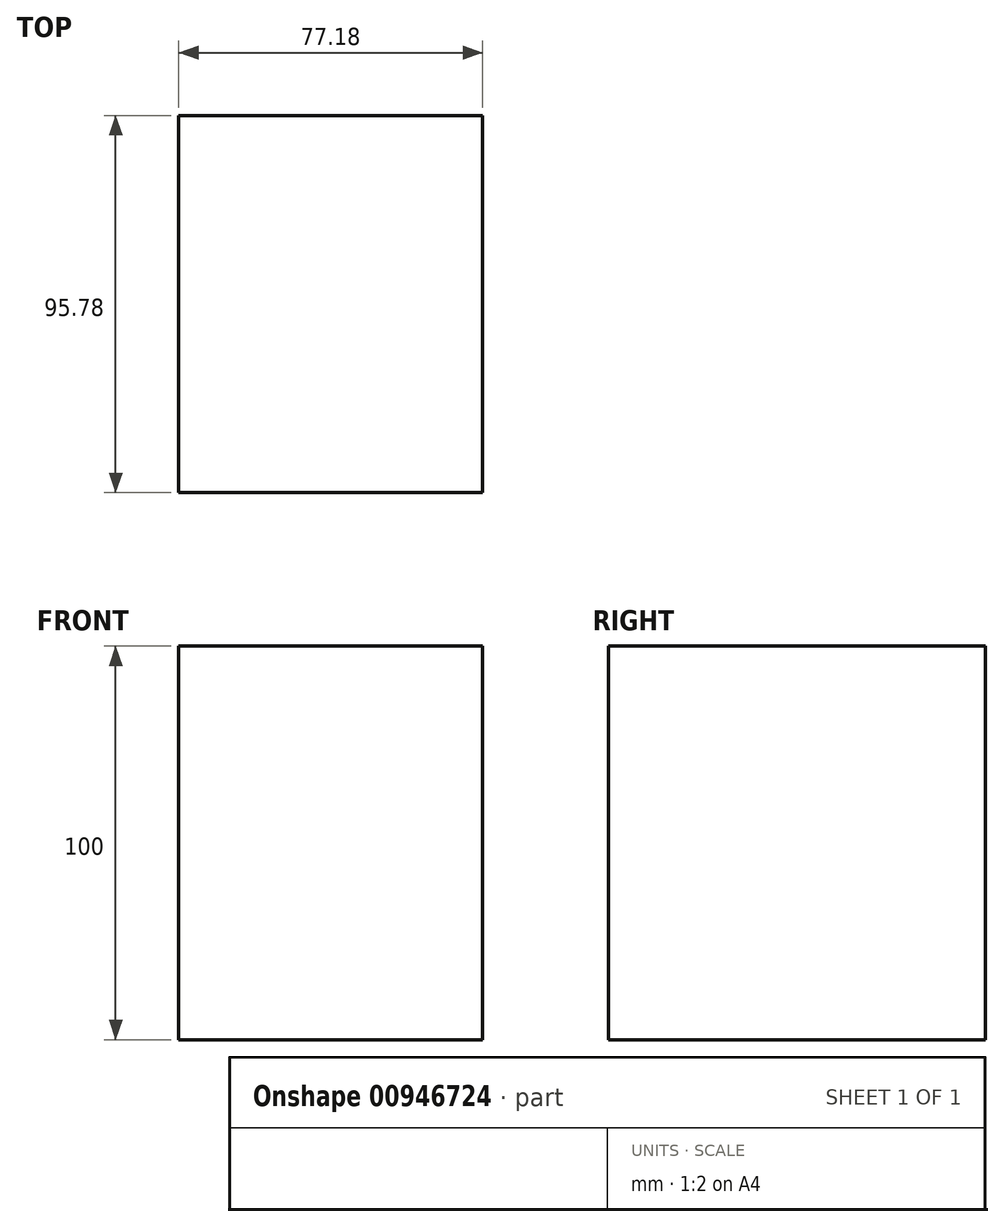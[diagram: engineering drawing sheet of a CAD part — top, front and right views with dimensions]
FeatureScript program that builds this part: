
annotation { "Feature Type Name" : "Feature", "Feature Type Description" : "" }
export const myFeature = defineFeature(function(context is Context, id is Id, definition is map)
    precondition{}
    {
        {
            var Q0;
            Q0=qCreatedBy(makeId("Top.planeOp"),FACE);
            var sketch = newSketch(context, id + "F0", { "sketchPlane" : qUnion([Q0])});
            skLineSegment(sketch, "E0.bottom", {"start": v(0, 0) * mm, "end": v(77.18, 0) * mm});
            skLineSegment(sketch, "E0.top", {"start": v(0, 95.78) * mm, "end": v(77.18, 95.78) * mm});
            skLineSegment(sketch, "E0.left", {"start": v(0, 0) * mm, "end": v(0, 95.78) * mm});
            skLineSegment(sketch, "E0.right", {"start": v(77.18, 0) * mm, "end": v(77.18, 95.78) * mm});
            skSolve(sketch);
        }
        {
            var Q0;
            Q0 = qSketchRegion(id + "F0", true);
            extrude(context, id + "F1", {"entities" : qUnion([Q0]), "depth" : 100 * mm, "offsetDistance" : 25 * mm});
        }
    });
